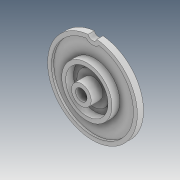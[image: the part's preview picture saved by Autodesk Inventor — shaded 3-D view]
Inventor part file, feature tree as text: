
AUTODESK INVENTOR PART (.ipt)
format: ipt  version: 2020 (Build 240168000, 168)  size: 159,232 bytes
history: native  units: mm
features: extrude x8, sketch x8, plane x2
ambient origin geometry x8: Origin, YZ Plane, XZ Plane, XY Plane, X Axis, Y Axis, Z Axis, Center Point
bodies: Solid1 (feature_tree)
feature tree (18):
  extrude  "Extrusion1"  Depth=1.0mm TaperAngle=0.0deg
  plane  "Work Plane1"
  extrude  "Extrusion3"  Depth=10.75mm
  plane  "Work Plane2"
  extrude  "Extrusion5"  Depth=2.0mm
  extrude  "Extrusion6"  Depth=0.4mm
  extrude  "Pressguide"  Depth=10.0mm
  extrude  "Extrusion8"  Depth=3.0mm
  extrude  "Extrusion9"  Depth=3.0mm TaperAngle=0.0deg
  extrude  "Axle"  Depth=0.57mm TaperAngle=0.0deg
  sketch  "Sketch1"  dims[d0=22.8mm d1=1.0mm d2=0.0mm]
  sketch  "Sketch3"  dims[d6=12.75mm d7=10.75mm]
  sketch  "Sketch5"  dims[d8=2.0mm d9=0.0mm d14=8.25mm]
  sketch  "Sketch6"  dims[d15=0.4mm d16=0.0mm d17=2.9mm]
  sketch  "Sketch7"  dims[d18=10.0mm d19=0.0mm d20=5.0mm]
  sketch  "Sketch8"  dims[d21=3.0mm d22=0.0mm d23=2.2mm]
  sketch  "Sketch9"  dims[d24=0.8mm d25=3.0mm d26=0.0mm]
  sketch  "Sketch10"  dims[d27=1.0mm d28=0.57mm d29=0.0mm d30=25.0mm d31=0.0mm]
